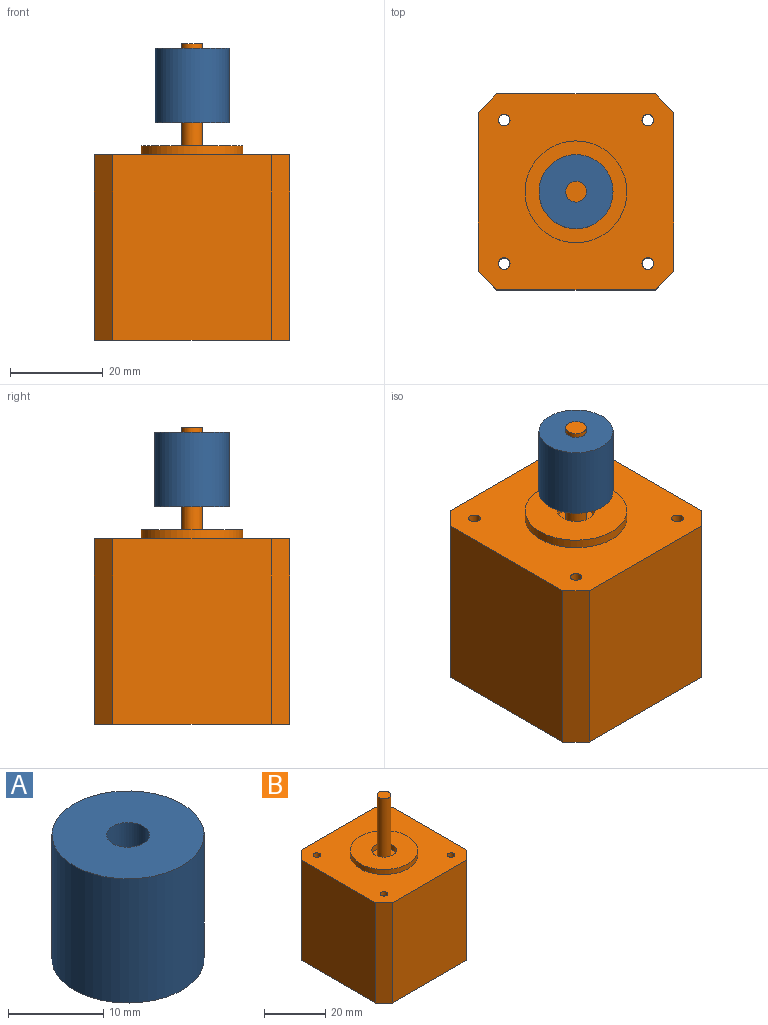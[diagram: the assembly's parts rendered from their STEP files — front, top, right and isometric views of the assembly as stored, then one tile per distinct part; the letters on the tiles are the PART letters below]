
ASSEMBLY  parts=2 mates=1
PART A: 4 faces, bbox 16x16x16 mm
  f0: cylinder r=2.25mm len=16mm, axis (0,0,-1), area 226.2mm2, adj f2,f3
  f1: cylinder r=8mm len=16mm, axis (0,0,-1), area 804.2mm2, adj f2,f3
  f2: plane 16x16mm, normal (0,0,1), area 185.2mm2, adj f0,f1
  f3: plane 16x16mm, normal (0,0,-1), area 185.2mm2, adj f0,f1
PART B: 20 faces, bbox 42.3x42.3x64 mm
  f0: plane 40x34.3mm, normal (0,-1,0), area 1372mm2, adj f4,f5,f14,f15
  f1: plane 40x34.3mm, normal (1,0,0), area 1372mm2, adj f4,f5,f13,f14
  f2: plane 40x34.3mm, normal (0,1,0), area 1372mm2, adj f4,f5,f12,f13
  f3: plane 40x34.3mm, normal (-1,0,0), area 1372mm2, adj f4,f5,f12,f15
  f4: plane 42.3x42.3mm, normal (0,0,1), area 1357.5mm2, adj f0,f1,f2,f3,f7,f12,f13,f14
  f5: plane 42.3x42.3mm, normal (0,0,-1), area 1737.7mm2, adj f0,f1,f2,f3,f12,f13,f14,f15
  f6: cylinder r=4mm len=8mm, axis (0,0,-1), area 50.3mm2, adj f8,f9
  f7: cylinder r=11mm len=22mm, axis (0,0,-1), area 138.2mm2, adj f4,f8
  f8: plane 22x22mm, normal (0,0,1), area 329.9mm2, adj f6,f7
  f9: plane 8x8mm, normal (0,0,1), area 34.4mm2, adj f6,f10
  f10: cylinder r=2.25mm len=24mm, axis (0,0,-1), area 339.3mm2, adj f9,f11
  f11: plane 4.5x4.5mm, normal (0,0,1), area 15.9mm2, adj f10
  f12: plane 40x4mm, normal (-0.71,0.71,0), area 226.3mm2, adj f2,f3,f4,f5
  f13: plane 40x4mm, normal (0.71,0.71,0), area 226.3mm2, adj f1,f2,f4,f5
  f14: plane 40x4mm, normal (0.71,-0.71,0), area 226.3mm2, adj f0,f1,f4,f5
  f15: plane 40x4mm, normal (-0.71,-0.71,0), area 226.3mm2, adj f0,f3,f4,f5
  f16: cylinder r=1.25mm len=40mm, axis (0,0,-1), area 314.2mm2, adj f4,f5
  f17: cylinder r=1.25mm len=40mm, axis (0,0,-1), area 314.2mm2, adj f4,f5
  f18: cylinder r=1.25mm len=40mm, axis (0,0,-1), area 314.2mm2, adj f4,f5
  f19: cylinder r=1.25mm len=40mm, axis (0,0,-1), area 314.2mm2, adj f4,f5
PLACE A t=(0,0,47)mm
PLACE B at identity
MATE fastened A.f1 <-> B.f10  axis (0,0,1) through (0,0,63)mm
